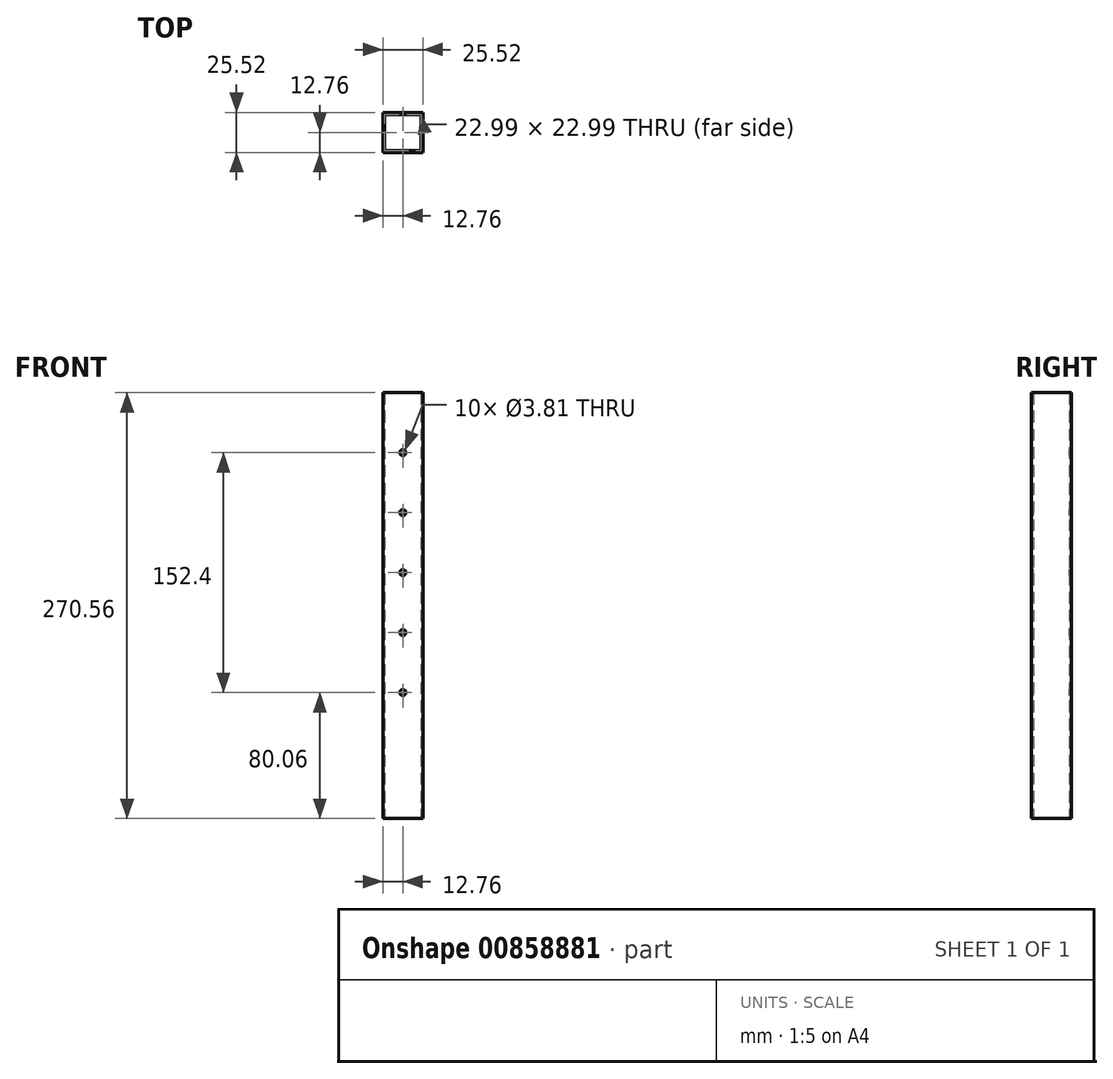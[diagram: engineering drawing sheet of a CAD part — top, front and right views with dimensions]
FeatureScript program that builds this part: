
annotation { "Feature Type Name" : "Feature", "Feature Type Description" : "" }
export const myFeature = defineFeature(function(context is Context, id is Id, definition is map)
    precondition{}
    {
        {
            var Q0;
            Q0=qCreatedBy(makeId("Top.planeOp"),FACE);
            var sketch = newSketch(context, id + "F0", { "sketchPlane" : qUnion([Q0])});
            skLineSegment(sketch, "E0.bottom", {"start": v(12.76, 12.76) * mm, "end": v(-12.76, 12.76) * mm});
            skLineSegment(sketch, "E0.top", {"start": v(12.76, -12.76) * mm, "end": v(-12.76, -12.76) * mm});
            skLineSegment(sketch, "E0.left", {"start": v(12.76, 12.76) * mm, "end": v(12.76, -12.76) * mm});
            skLineSegment(sketch, "E0.right", {"start": v(-12.76, 12.76) * mm, "end": v(-12.76, -12.76) * mm});
            skPoint(sketch, "E0.middle", {"position": v(0, 0) * mm});
            skLineSegment(sketch, "E1.bottom", {"start": v(11.5, 11.5) * mm, "end": v(-11.5, 11.5) * mm});
            skLineSegment(sketch, "E1.top", {"start": v(11.5, -11.5) * mm, "end": v(-11.5, -11.5) * mm});
            skLineSegment(sketch, "E1.left", {"start": v(11.5, 11.5) * mm, "end": v(11.5, -11.5) * mm});
            skLineSegment(sketch, "E1.right", {"start": v(-11.5, 11.5) * mm, "end": v(-11.5, -11.5) * mm});
            skSolve(sketch);
        }
        {
            var Q0;
            Q0 = qSketchRegion(id + "F0", true);
            extrude(context, id + "F1", {"entities" : qUnion([Q0]), "depth" : 228.6 * mm, "offsetDistance" : 25.4 * mm});
        }
        {
            var Q0;
            Q0=makeQuery(id+"F1.opExtrude","SWEPT_FACE",FACE,{"disambiguationData":[OSD([sQuery(id+"F0.wireOp",EDGE,"E0.top")])]});
            var sketch = newSketch(context, id + "F2", { "sketchPlane" : qUnion([Q0])});
            skCircle(sketch, "E2", {"center": v(0, 38.1) * mm, "radius": 1.9 * mm});
            skCircle(sketch, "E3.0.1.0", {"center": v(0, 76.2) * mm, "radius": 1.9 * mm});
            skCircle(sketch, "E3.0.2.0", {"center": v(0, 114.3) * mm, "radius": 1.9 * mm});
            skCircle(sketch, "E3.0.3.0", {"center": v(0, 152.4) * mm, "radius": 1.9 * mm});
            skCircle(sketch, "E3.0.4.0", {"center": v(0, 190.5) * mm, "radius": 1.9 * mm});
            skLineSegment(sketch, "E3.direction1", {"start": v(0, 38.1) * mm, "end": v(25.4, 38.1) * mm, "construction": true});
            skLineSegment(sketch, "E3.direction2", {"start": v(0, 38.1) * mm, "end": v(0, 76.2) * mm, "construction": true});
            skSolve(sketch);
        }
        {
            var Q0;
            Q0 = qSketchRegion(id + "F2", true);
            extrude(context, id + "F3", {"entities" : qUnion([Q0]), "operationType" : NewBodyOperationType.REMOVE, "endBound" : BoundingType.THROUGH_ALL, "oppositeDirection" : true, "depth" : 25.4 * mm, "offsetDistance" : 25.4 * mm});
        }
        {
            var Q0;
            Q0=makeQuery(id+"F1.opExtrude","CAP_FACE",FACE,{"disambiguationData":[OSD([sQuery(id+"F0.wireOp",EDGE,"E0.bottom"),sQuery(id+"F0.wireOp",EDGE,"E0.top"),sQuery(id+"F0.wireOp",EDGE,"E0.left"),sQuery(id+"F0.wireOp",EDGE,"E0.right"),sQuery(id+"F0.wireOp",EDGE,"E1.bottom"),sQuery(id+"F0.wireOp",EDGE,"E1.top"),sQuery(id+"F0.wireOp",EDGE,"E1.left"),sQuery(id+"F0.wireOp",EDGE,"E1.right")])],"isStart":true});
            var sketch = newSketch(context, id + "F4", { "sketchPlane" : qUnion([Q0])});
            skLineSegment(sketch, "E4.bottom", {"start": v(12.76, 12.76) * mm, "end": v(-12.76, 12.76) * mm});
            skLineSegment(sketch, "E4.top", {"start": v(12.76, -12.76) * mm, "end": v(-12.76, -12.76) * mm});
            skLineSegment(sketch, "E4.left", {"start": v(12.76, 12.76) * mm, "end": v(12.76, -12.76) * mm});
            skLineSegment(sketch, "E4.right", {"start": v(-12.76, 12.76) * mm, "end": v(-12.76, -12.76) * mm});
            skPoint(sketch, "E4.middle", {"position": v(0, 0) * mm});
            skLineSegment(sketch, "E5.bottom", {"start": v(11.5, 11.5) * mm, "end": v(-11.5, 11.5) * mm});
            skLineSegment(sketch, "E5.top", {"start": v(11.5, -11.5) * mm, "end": v(-11.5, -11.5) * mm});
            skLineSegment(sketch, "E5.left", {"start": v(11.5, 11.5) * mm, "end": v(11.5, -11.5) * mm});
            skLineSegment(sketch, "E5.right", {"start": v(-11.5, 11.5) * mm, "end": v(-11.5, -11.5) * mm});
            skSolve(sketch);
        }
        {
            var Q0;
            Q0 = qSketchRegion(id + "F4", true);
            extrude(context, id + "F5", {"entities" : qUnion([Q0]), "operationType" : NewBodyOperationType.ADD, "depth" : 41.96 * mm, "offsetDistance" : 25.4 * mm});
        }
    });
